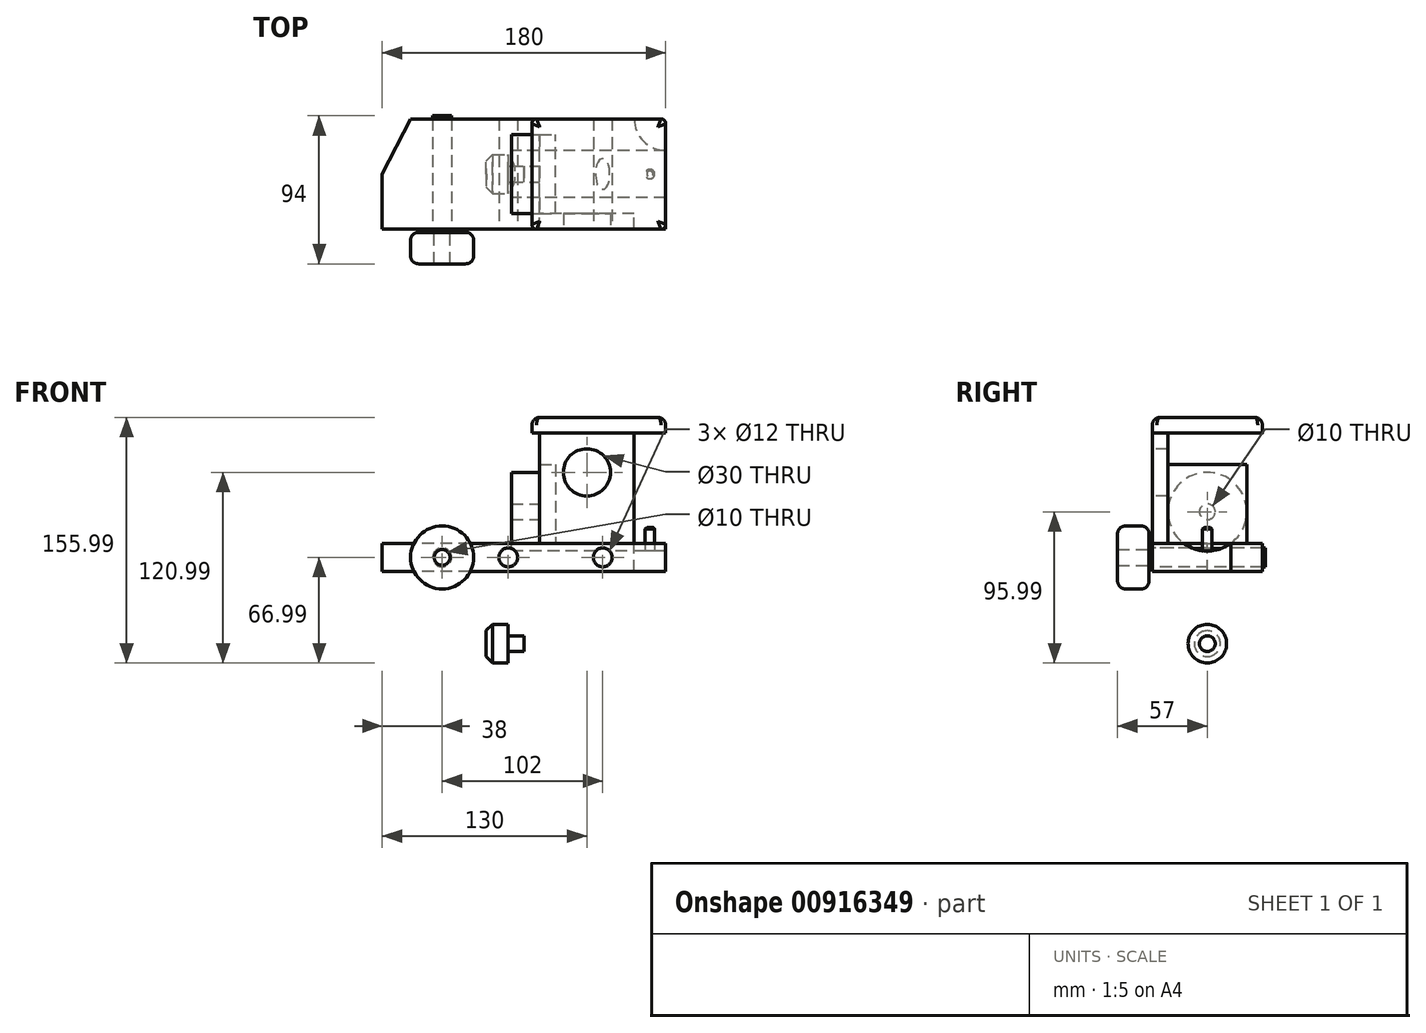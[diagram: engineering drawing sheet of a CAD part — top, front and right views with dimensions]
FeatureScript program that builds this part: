
annotation { "Feature Type Name" : "Feature", "Feature Type Description" : "" }
export const myFeature = defineFeature(function(context is Context, id is Id, definition is map)
    precondition{}
    {
        {
            var Q0;
            Q0=qCreatedBy(makeId("Top.planeOp"),FACE);
            var sketch = newSketch(context, id + "F0", { "sketchPlane" : qUnion([Q0])});
            skLineSegment(sketch, "E0.bottom", {"start": v(90, 35) * mm, "end": v(-90, 35) * mm});
            skLineSegment(sketch, "E0.top", {"start": v(90, -35) * mm, "end": v(-90, -35) * mm});
            skLineSegment(sketch, "E0.left", {"start": v(90, 35) * mm, "end": v(90, -35) * mm});
            skLineSegment(sketch, "E0.right", {"start": v(-90, 35) * mm, "end": v(-90, -35) * mm});
            skPoint(sketch, "E0.middle", {"position": v(0, 0) * mm});
            skSolve(sketch);
        }
        {
            var Q0;
            Q0 = qSketchRegion(id + "F0", true);
            extrude(context, id + "F1", {"entities" : qUnion([Q0]), "depth" : 18 * mm, "offsetDistance" : 25 * mm});
        }
        {
            var Q0;
            Q0=makeQuery(id+"F1.opExtrude","CAP_FACE",FACE,{"disambiguationData":[OSD([sQuery(id+"F0.wireOp",EDGE,"E0.bottom"),sQuery(id+"F0.wireOp",EDGE,"E0.top"),sQuery(id+"F0.wireOp",EDGE,"E0.left"),sQuery(id+"F0.wireOp",EDGE,"E0.right")])],"isStart":false});
            var sketch = newSketch(context, id + "F2", { "sketchPlane" : qUnion([Q0])});
            skLineSegment(sketch, "E1", {"start": v(-90, 0) * mm, "end": v(-72, 35) * mm});
            skLineSegment(sketch, "E2", {"start": v(-72, 35) * mm, "end": v(-90, 35) * mm});
            skLineSegment(sketch, "E3", {"start": v(-90, 35) * mm, "end": v(-90, 0) * mm});
            skCircle(sketch, "E4", {"center": v(90, 35) * mm, "radius": 20 * mm});
            skSolve(sketch);
        }
        {
            var Q0;
            Q0 = qSketchRegion(id + "F2", true);
            extrude(context, id + "F3", {"entities" : qUnion([Q0]), "operationType" : NewBodyOperationType.REMOVE, "endBound" : BoundingType.THROUGH_ALL, "oppositeDirection" : true, "depth" : 25 * mm, "offsetDistance" : 25 * mm});
        }
        {
            var Q0;
            Q0=makeQuery(id+"F1.opExtrude","CAP_FACE",FACE,{"disambiguationData":[OSD([sQuery(id+"F0.wireOp",EDGE,"E0.bottom"),sQuery(id+"F0.wireOp",EDGE,"E0.top"),sQuery(id+"F0.wireOp",EDGE,"E0.left"),sQuery(id+"F0.wireOp",EDGE,"E0.right")])],"isStart":false});
            var sketch = newSketch(context, id + "F4", { "sketchPlane" : qUnion([Q0])});
            skCircle(sketch, "E5", {"center": v(80, 0) * mm, "radius": 3 * mm});
            skSolve(sketch);
        }
        {
            var Q0;
            Q0 = qSketchRegion(id + "F4", true);
            extrude(context, id + "F5", {"entities" : qUnion([Q0]), "operationType" : NewBodyOperationType.REMOVE, "oppositeDirection" : true, "depth" : 10 * mm, "offsetDistance" : 25 * mm});
        }
        {
            var Q0;
            Q0=makeQuery(id+"F1.opExtrude","SWEPT_FACE",FACE,{"disambiguationData":[OSD([sQuery(id+"F0.wireOp",EDGE,"E0.top")])]});
            var sketch = newSketch(context, id + "F6", { "sketchPlane" : qUnion([Q0])});
            skCircle(sketch, "E6", {"center": v(-52, 9) * mm, "radius": 6 * mm});
            skPoint(sketch, "E6.centerSnap0", {"position": v(-72, 9) * mm});
            skCircle(sketch, "E7", {"center": v(-10, 9) * mm, "radius": 6 * mm});
            skCircle(sketch, "E8", {"center": v(50, 9) * mm, "radius": 6 * mm});
            skSolve(sketch);
        }
        {
            var Q0;
            Q0 = qSketchRegion(id + "F6", true);
            extrude(context, id + "F7", {"entities" : qUnion([Q0]), "operationType" : NewBodyOperationType.REMOVE, "endBound" : BoundingType.THROUGH_ALL, "oppositeDirection" : true, "depth" : 25 * mm, "offsetDistance" : 25 * mm});
        }
        {
            var Q0;
            Q0=makeQuery(id+"F1.opExtrude","CAP_FACE",FACE,{"disambiguationData":[OSD([sQuery(id+"F0.wireOp",EDGE,"E0.bottom"),sQuery(id+"F0.wireOp",EDGE,"E0.top"),sQuery(id+"F0.wireOp",EDGE,"E0.left"),sQuery(id+"F0.wireOp",EDGE,"E0.right")])],"isStart":false});
            var sketch = newSketch(context, id + "F8", { "sketchPlane" : qUnion([Q0])});
            skPoint(sketch, "E9.oppositeSnap0", {"position": v(85.86, -25) * mm});
            skLineSegment(sketch, "E9.bottom", {"start": v(70, -35) * mm, "end": v(10, -35) * mm});
            skLineSegment(sketch, "E9.top", {"start": v(70, -25) * mm, "end": v(10, -25) * mm});
            skLineSegment(sketch, "E9.left", {"start": v(70, -35) * mm, "end": v(70, -25) * mm});
            skLineSegment(sketch, "E9.right", {"start": v(10, -35) * mm, "end": v(10, -25) * mm});
            skSolve(sketch);
        }
        {
            var Q0;
            Q0 = qSketchRegion(id + "F8", true);
            extrude(context, id + "F9", {"entities" : qUnion([Q0]), "depth" : 70 * mm, "offsetDistance" : 25 * mm});
        }
        {
            var Q0;
            Q0=makeQuery(id+"F1.opExtrude","CAP_FACE",FACE,{"disambiguationData":[OSD([sQuery(id+"F0.wireOp",EDGE,"E0.bottom"),sQuery(id+"F0.wireOp",EDGE,"E0.top"),sQuery(id+"F0.wireOp",EDGE,"E0.left"),sQuery(id+"F0.wireOp",EDGE,"E0.right")])],"isStart":false});
            var sketch = newSketch(context, id + "F10", { "sketchPlane" : qUnion([Q0])});
            skLineSegment(sketch, "E10.bottom", {"start": v(10, -25) * mm, "end": v(20, -25) * mm});
            skLineSegment(sketch, "E10.top", {"start": v(10, 25) * mm, "end": v(20, 25) * mm});
            skLineSegment(sketch, "E10.left", {"start": v(10, -25) * mm, "end": v(10, 25) * mm});
            skLineSegment(sketch, "E10.right", {"start": v(20, -25) * mm, "end": v(20, 25) * mm});
            skSolve(sketch);
        }
        {
            var Q0;
            Q0 = qSketchRegion(id + "F10", true);
            extrude(context, id + "F11", {"entities" : qUnion([Q0]), "depth" : 50 * mm, "offsetDistance" : 25 * mm});
        }
        {
            var Q0;
            Q0=makeQuery(id+"F11.opExtrude","SWEPT_FACE",FACE,{"disambiguationData":[OSD([sQuery(id+"F10.wireOp",EDGE,"E10.left")])]});
            var sketch = newSketch(context, id + "F12", { "sketchPlane" : qUnion([Q0])});
            skCircle(sketch, "E11", {"center": v(0, 38) * mm, "radius": 25 * mm});
            skPoint(sketch, "E11.centerSnap0", {"position": v(0, 18) * mm});
            skCircle(sketch, "E12", {"center": v(0, 38) * mm, "radius": 5 * mm});
            skSolve(sketch);
        }
        {
            var Q0;
            Q0 = qSketchRegion(id + "F12", true);
            extrude(context, id + "F13", {"entities" : qUnion([Q0]), "depth" : 18 * mm, "offsetDistance" : 25 * mm});
        }
        {
            var Q0;
            Q0=makeQuery(id+"F13.opExtrude","CAP_FACE",FACE,{"disambiguationData":[OSD([sQuery(id+"F12.wireOp",EDGE,"E11")])],"isStart":false});
            var sketch = newSketch(context, id + "F14", { "sketchPlane" : qUnion([Q0])});
            skLineSegment(sketch, "E13.0", {"start": v(25, 18) * mm, "end": v(-25, 18) * mm});
            skSolve(sketch);
        }
        {
            var Q0;
            Q0 = qSketchRegion(id + "F14", true);
            var Q1;
            {var subQ0=sQuery(id+"F14.wireOp",EDGE,"E13.0");var subQ1=makeQuery(id+"F13.opExtrude","CAP_EDGE",EDGE,{"disambiguationData":[OSD([sQuery(id+"F12.wireOp",EDGE,"E11")])],"isStart":false});var subQ2=makeQuery(id+"F14.imprint","INTERSECT",VERTEX,{"disambiguationData":[OD(0.0)],"derivedFrom":[subQ1,subQ0]});Q1=makeQuery(id+"F14.imprint","IMPRINT",FACE,{"disambiguationData":[TD([[makeQuery(id+"F14.imprint","IMPRINT",EDGE,{"disambiguationData":[TD([[subQ2,-1.0]])],"derivedFrom":subQ0}),1.0]])]});}
            extrude(context, id + "F15", {"entities" : qUnion([Q0, Q1]), "operationType" : NewBodyOperationType.REMOVE, "endBound" : BoundingType.THROUGH_ALL, "oppositeDirection" : true, "depth" : 25 * mm, "offsetDistance" : 25 * mm});
        }
        {
            var Q0;
            Q0=makeQuery(id+"F9.opExtrude","CAP_FACE",FACE,{"disambiguationData":[OSD([sQuery(id+"F8.wireOp",EDGE,"E9.bottom"),sQuery(id+"F8.wireOp",EDGE,"E9.top"),sQuery(id+"F8.wireOp",EDGE,"E9.left"),sQuery(id+"F8.wireOp",EDGE,"E9.right")])],"isStart":false});
            var sketch = newSketch(context, id + "F16", { "sketchPlane" : qUnion([Q0])});
            skLineSegment(sketch, "E14.bottom", {"start": v(90, -35) * mm, "end": v(5, -35) * mm});
            skLineSegment(sketch, "E14.top", {"start": v(90, 35) * mm, "end": v(5, 35) * mm});
            skLineSegment(sketch, "E14.left", {"start": v(90, -35) * mm, "end": v(90, 35) * mm});
            skLineSegment(sketch, "E14.right", {"start": v(5, -35) * mm, "end": v(5, 35) * mm});
            skPoint(sketch, "E14.middle", {"position": v(47.5, 0) * mm});
            skSolve(sketch);
        }
        {
            var Q0;
            Q0 = qSketchRegion(id + "F16", true);
            extrude(context, id + "F17", {"entities" : qUnion([Q0]), "depth" : 10 * mm, "offsetDistance" : 25 * mm});
        }
        {
            var Q0;
            Q0=makeQuery(id+"F17.opExtrude","SWEPT_EDGE",EDGE,{"disambiguationData":[OSD([sQuery(id+"F16.wireOp",EDGE,"E14.top"),sQuery(id+"F16.wireOp",EDGE,"E14.right")])]});
            var Q1;
            Q1=makeQuery(id+"F17.opExtrude","SWEPT_EDGE",EDGE,{"disambiguationData":[OSD([sQuery(id+"F16.wireOp",EDGE,"E14.top"),sQuery(id+"F16.wireOp",EDGE,"E14.left")])]});
            var Q2;
            Q2=makeQuery(id+"F17.opExtrude","SWEPT_EDGE",EDGE,{"disambiguationData":[OSD([sQuery(id+"F16.wireOp",EDGE,"E14.bottom"),sQuery(id+"F16.wireOp",EDGE,"E14.left")])]});
            var Q3;
            Q3=makeQuery(id+"F17.opExtrude","SWEPT_EDGE",EDGE,{"disambiguationData":[OSD([sQuery(id+"F16.wireOp",EDGE,"E14.bottom"),sQuery(id+"F16.wireOp",EDGE,"E14.right")])]});
            fillet(context, id + "F18", {"entities" : qUnion([Q0, Q1, Q2, Q3]), "radius" : 3 * mm, "tangentPropagation" : true, "allowEdgeOverflow" : false});
        }
        {
            var Q0;
            Q0=makeQuery(id+"F17.opExtrude","CAP_FACE",FACE,{"disambiguationData":[OSD([sQuery(id+"F16.wireOp",EDGE,"E14.bottom"),sQuery(id+"F16.wireOp",EDGE,"E14.top"),sQuery(id+"F16.wireOp",EDGE,"E14.left"),sQuery(id+"F16.wireOp",EDGE,"E14.right")])],"isStart":false});
            fillet(context, id + "F19", {"entities" : qUnion([Q0]), "radius" : 5 * mm, "tangentPropagation" : true, "allowEdgeOverflow" : false});
        }
        {
            var Q0;
            Q0=makeQuery(id+"F9.opExtrude","SWEPT_FACE",FACE,{"disambiguationData":[OSD([sQuery(id+"F8.wireOp",EDGE,"E9.bottom")])]});
            var sketch = newSketch(context, id + "F20", { "sketchPlane" : qUnion([Q0])});
            skLineSegment(sketch, "E15", {"start": v(10, 18) * mm, "end": v(70, 88) * mm, "construction": true});
            skCircle(sketch, "E16", {"center": v(40, 63) * mm, "radius": 15 * mm});
            skPoint(sketch, "E16.centerSnap0", {"position": v(40, 53) * mm});
            skSolve(sketch);
        }
        {
            var Q0;
            Q0 = qSketchRegion(id + "F20", true);
            extrude(context, id + "F21", {"entities" : qUnion([Q0]), "operationType" : NewBodyOperationType.REMOVE, "endBound" : BoundingType.THROUGH_ALL, "oppositeDirection" : true, "depth" : 25 * mm, "offsetDistance" : 25 * mm});
        }
        {
            var Q0;
            Q0=qCreatedBy(makeId("Front.planeOp"),FACE);
            var sketch = newSketch(context, id + "F22", { "sketchPlane" : qUnion([Q0])});
            skCircle(sketch, "E17.0", {"center": v(-52, 9) * mm, "radius": 6 * mm});
            skSolve(sketch);
        }
        {
            var Q0;
            Q0 = qSketchRegion(id + "F22", true);
            extrude(context, id + "F23", {"entities" : qUnion([Q0]), "endBound" : BoundingType.SYMMETRIC, "depth" : 74 * mm, "offsetDistance" : 25 * mm});
        }
        {
            var Q0;
            Q0=makeQuery(id+"F23.opExtrude","CAP_FACE",FACE,{"disambiguationData":[OSD([sQuery(id+"F22.wireOp",EDGE,"E17.0")])],"isStart":false});
            var sketch = newSketch(context, id + "F24", { "sketchPlane" : qUnion([Q0])});
            skCircle(sketch, "E18", {"center": v(-52, 9) * mm, "radius": 5 * mm});
            skSolve(sketch);
        }
        {
            var Q0;
            Q0 = qSketchRegion(id + "F24", true);
            extrude(context, id + "F25", {"entities" : qUnion([Q0]), "operationType" : NewBodyOperationType.ADD, "depth" : 20 * mm, "offsetDistance" : 25 * mm});
        }
        {
            var Q0;
            Q0=makeQuery(id+"F5.boolean.opBoolean","COPY",FACE,{"derivedFrom":makeQuery(id+"F5.opExtrude","CAP_FACE",FACE,{"disambiguationData":[OSD([sQuery(id+"F4.wireOp",EDGE,"E5")])],"isStart":false})});
            var sketch = newSketch(context, id + "F26", { "sketchPlane" : qUnion([Q0])});
            skCircle(sketch, "E19.0", {"center": v(80, 0) * mm, "radius": 3 * mm});
            skSolve(sketch);
        }
        {
            var Q0;
            Q0 = qSketchRegion(id + "F26", true);
            extrude(context, id + "F27", {"entities" : qUnion([Q0]), "operationType" : NewBodyOperationType.ADD, "depth" : 20 * mm, "offsetDistance" : 25 * mm});
        }
        {
            var Q0;
            Q0=makeQuery(id+"F27.opExtrude","CAP_EDGE",EDGE,{"disambiguationData":[OSD([sQuery(id+"F26.wireOp",EDGE,"E19.0")])],"isStart":false});
            chamfer(context, id + "F28", {"entities" : qUnion([Q0]), "width" : 1 * mm, "tangentPropagation" : true});
        }
        {
            var Q0;
            Q0=makeQuery(id+"F23.opExtrude","CAP_FACE",FACE,{"disambiguationData":[OSD([sQuery(id+"F22.wireOp",EDGE,"E17.0")])],"isStart":false});
            var sketch = newSketch(context, id + "F29", { "sketchPlane" : qUnion([Q0])});
            skCircle(sketch, "E20.0", {"center": v(-52, 9) * mm, "radius": 5 * mm});
            skCircle(sketch, "E21", {"center": v(-52, 9) * mm, "radius": 20 * mm});
            skSolve(sketch);
        }
        {
            var Q0;
            Q0 = qSketchRegion(id + "F29", true);
            extrude(context, id + "F30", {"entities" : qUnion([Q0]), "depth" : 20 * mm, "offsetDistance" : 25 * mm});
        }
        {
            var Q0;
            Q0=makeQuery(id+"F30.opExtrude","CAP_EDGE",EDGE,{"disambiguationData":[OSD([sQuery(id+"F29.wireOp",EDGE,"E21")])],"isStart":false});
            var Q1;
            Q1=makeQuery(id+"F30.opExtrude","CAP_EDGE",EDGE,{"disambiguationData":[OSD([sQuery(id+"F29.wireOp",EDGE,"E21")])],"isStart":true});
            fillet(context, id + "F31", {"entities" : qUnion([Q0, Q1]), "radius" : 5 * mm, "tangentPropagation" : true, "allowEdgeOverflow" : false});
        }
        {
            var Q0;
            Q0=qCreatedBy(makeId("Front.planeOp"),FACE);
            var sketch = newSketch(context, id + "F32", { "sketchPlane" : qUnion([Q0])});
            skLineSegment(sketch, "E22", {"start": v(0, -40.76) * mm, "end": v(-10, -40.76) * mm});
            skLineSegment(sketch, "E23", {"start": v(-10, -40.76) * mm, "end": v(-10, -33.53) * mm});
            skLineSegment(sketch, "E24", {"start": v(-10, -33.53) * mm, "end": v(-20, -33.53) * mm});
            skLineSegment(sketch, "E25", {"start": v(-20, -33.53) * mm, "end": v(-24, -37.53) * mm});
            skLineSegment(sketch, "E26", {"start": v(-24, -37.53) * mm, "end": v(-23.83, -45.76) * mm});
            skLineSegment(sketch, "E27", {"start": v(0, -40.76) * mm, "end": v(0, -45.76) * mm});
            skLineSegment(sketch, "E28", {"start": v(0, -45.76) * mm, "end": v(-45.8, -45.76) * mm, "construction": true});
            skLineSegment(sketch, "E29", {"start": v(-23.83, -45.76) * mm, "end": v(0, -45.76) * mm});
            skSolve(sketch);
        }
        {
            var Q0;
            Q0 = qSketchRegion(id + "F32", true);
            var Q1;
            Q1=sQuery(id+"F32.wireOp",EDGE,"E28");
            revolve(context, id + "F33", {"surfaceOperationType" : NewSurfaceOperationType.NEW, "entities" : qUnion([Q0]), "axis" : qUnion([Q1]), "revolveType" : RevolveType.FULL});
        }
    });
